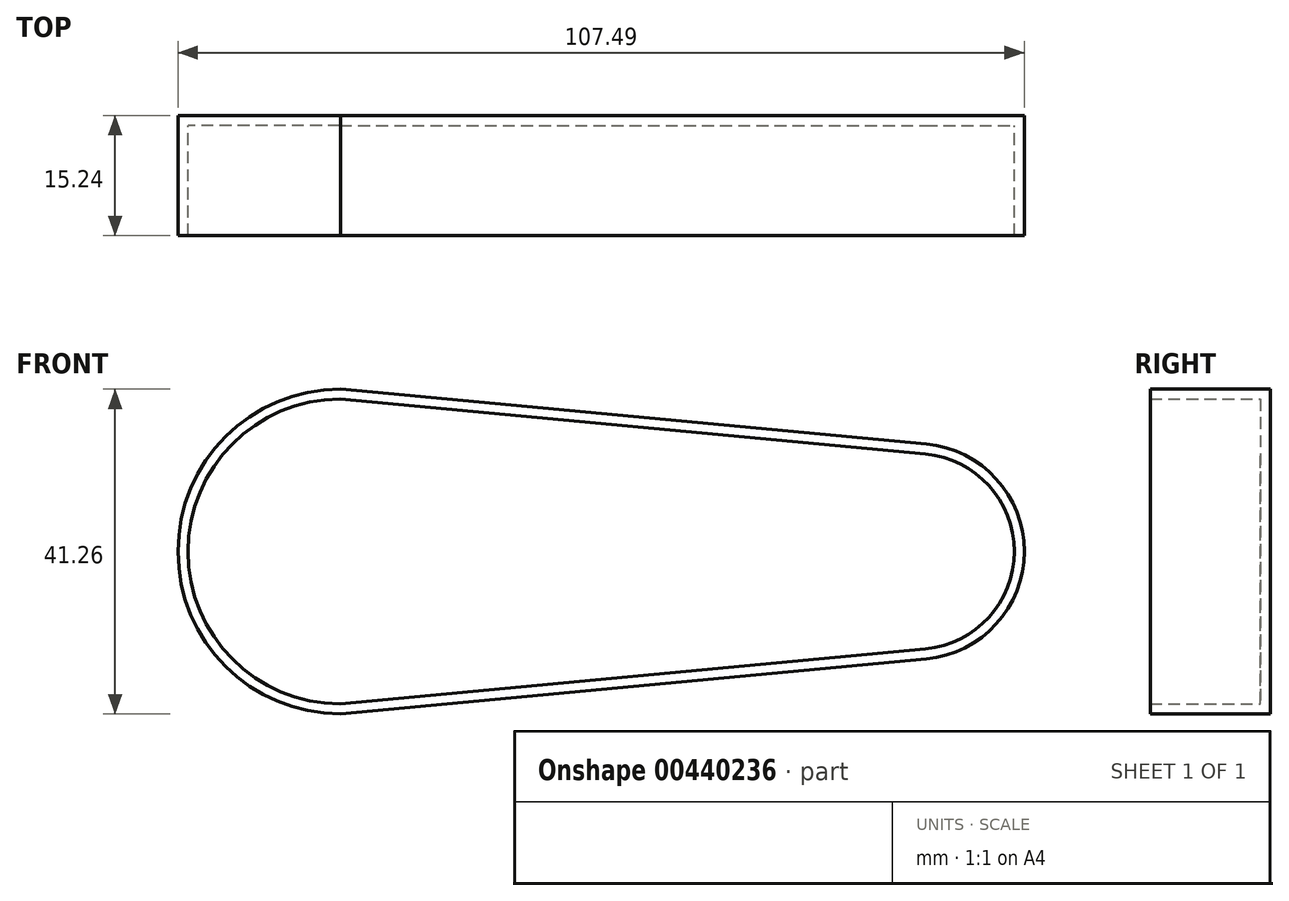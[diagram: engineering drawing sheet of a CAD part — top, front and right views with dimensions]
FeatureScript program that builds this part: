
annotation { "Feature Type Name" : "Feature", "Feature Type Description" : "" }
export const myFeature = defineFeature(function(context is Context, id is Id, definition is map)
    precondition{}
    {
        {
            var Q0;
            Q0=qCreatedBy(makeId("Front.planeOp"),FACE);
            var sketch = newSketch(context, id + "F0", { "sketchPlane" : qUnion([Q0])});
            skArc(sketch, "E0", {"start": v(3.84, 20.27) * mm, "mid": v(-20.63, 0) * mm, "end": v(3.84, -20.27) * mm});
            skArc(sketch, "E1", {"start": v(74.43, -13.64) * mm, "mid": v(86.86, 0) * mm, "end": v(74.43, 13.64) * mm});
            skLineSegment(sketch, "E2", {"start": v(0, -20.63) * mm, "end": v(74.43, -13.64) * mm});
            skLineSegment(sketch, "E3", {"start": v(0, 20.63) * mm, "end": v(74.43, 13.64) * mm});
            skSolve(sketch);
        }
        {
            var Q0;
            {var subQ3=sQuery(id+"F0.wireOp",EDGE,"E1");Q0=makeQuery(id+"F0.imprint","IMPRINT",FACE,{"disambiguationData":[TD([[makeQuery(id+"F0.imprint","IMPRINT",EDGE,{"derivedFrom":subQ3}),1.0]])]});}
            extrude(context, id + "F1", {"entities" : qUnion([Q0]), "depth" : 15.24 * mm});
        }
        {
            var Q0;
            Q0=makeQuery(id+"F1.opExtrude","CAP_FACE",FACE,{"disambiguationData":[OSD([sQuery(id+"F0.wireOp",EDGE,"E0"),sQuery(id+"F0.wireOp",EDGE,"E1"),sQuery(id+"F0.wireOp",EDGE,"E2"),sQuery(id+"F0.wireOp",EDGE,"E3")])],"isStart":false});
            shell(context, id + "F2", {"entities" : qUnion([Q0]), "thickness" : 1.27 * mm});
        }
    });
